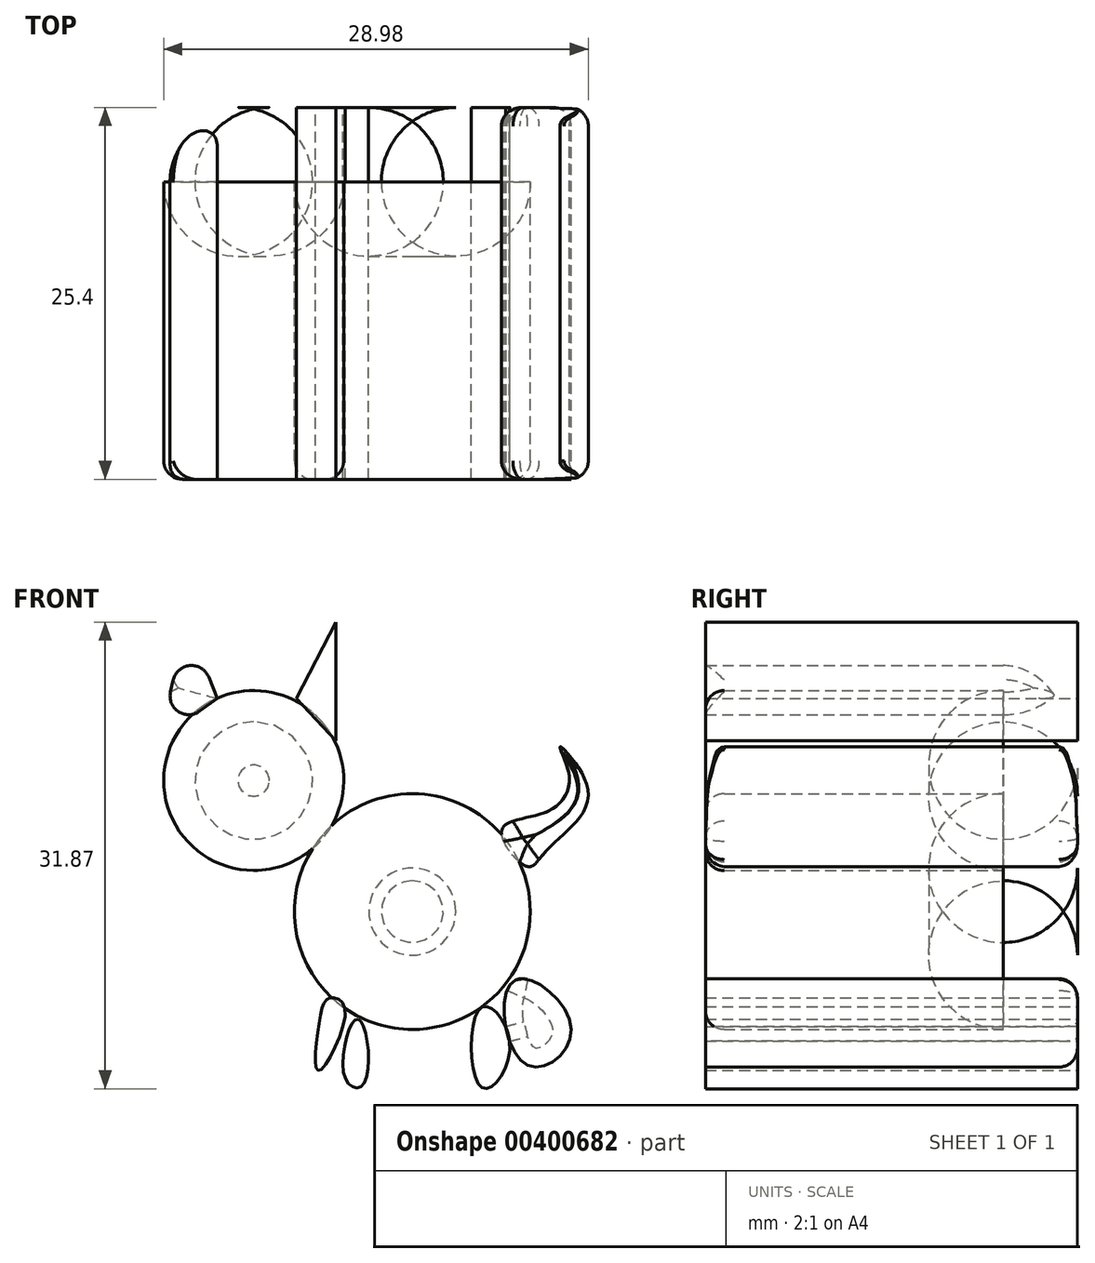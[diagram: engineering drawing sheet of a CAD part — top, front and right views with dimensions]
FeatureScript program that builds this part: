
annotation { "Feature Type Name" : "Feature", "Feature Type Description" : "" }
export const myFeature = defineFeature(function(context is Context, id is Id, definition is map)
    precondition{}
    {
        {
            var Q0;
            Q0=qCreatedBy(makeId("Front.planeOp"),FACE);
            var sketch = newSketch(context, id + "F0", { "sketchPlane" : qUnion([Q0])});
            skCircle(sketch, "E0", {"center": v(-53.48, 46.1) * mm, "radius": 6.14 * mm});
            skSolve(sketch);
        }
        {
            var Q0;
            Q0=qCreatedBy(makeId("Front.planeOp"),FACE);
            var sketch = newSketch(context, id + "F1", { "sketchPlane" : qUnion([Q0])});
            skLineSegment(sketch, "E1", {"start": v(-50.57, 51.7) * mm, "end": v(-47.86, 56.91) * mm});
            skLineSegment(sketch, "E2", {"start": v(-47.86, 48.8) * mm, "end": v(-47.86, 56.91) * mm});
            skLineSegment(sketch, "E3", {"start": v(-50.57, 51.7) * mm, "end": v(-47.86, 48.8) * mm});
            skLineSegment(sketch, "E4", {"start": v(-55.98, 51.7) * mm, "end": v(-58.06, 56.91) * mm});
            skLineSegment(sketch, "E5", {"start": v(-58.06, 56.91) * mm, "end": v(-59.93, 48.8) * mm});
            skLineSegment(sketch, "E6", {"start": v(-59.93, 48.8) * mm, "end": v(-55.98, 51.7) * mm});
            skSolve(sketch);
        }
        {
            var Q0;
            Q0=qCreatedBy(makeId("Front.planeOp"),FACE);
            var sketch = newSketch(context, id + "F2", { "sketchPlane" : qUnion([Q0])});
            skCircle(sketch, "E7", {"center": v(-42.65, 37.14) * mm, "radius": 8.05 * mm});
            skSolve(sketch);
        }
        {
            var Q0;
            Q0=qCreatedBy(makeId("Front.planeOp"),FACE);
            var sketch = newSketch(context, id + "F3", { "sketchPlane" : qUnion([Q0])});
            skFitSpline(sketch, "E8", {"points": [v(-48.28, 31.24) * mm, v(-48.97, 29.8) * mm, v(-49.04, 26.3) * mm, v(-47.25, 30.55) * mm, v(-48.28, 31.24) * mm]});
            skFitSpline(sketch, "E9", {"points": [v(-46.36, 29.8) * mm, v(-47.25, 25.81) * mm, v(-45.95, 25.4) * mm, v(-46.36, 29.8) * mm]});
            skFitSpline(sketch, "E10", {"points": [v(-37.98, 30.55) * mm, v(-37.92, 25.13) * mm, v(-36, 28) * mm, v(-37.98, 30.55) * mm]});
            skFitSpline(sketch, "E11", {"points": [v(-35.72, 32.4) * mm, v(-34.9, 26.7) * mm, v(-31.8, 29.1) * mm, v(-35.72, 32.4) * mm]});
            skFitSpline(sketch, "E12", {"points": [v(-36.54, 42.7) * mm, v(-33.52, 43.94) * mm, v(-31.94, 46.4) * mm, v(-32.56, 48.4) * mm, v(-30.91, 46.27) * mm, v(-31.12, 43.73) * mm, v(-33.73, 41.05) * mm, v(-34.83, 40.23) * mm, v(-36.54, 42.7) * mm]});
            skSolve(sketch);
        }
        {
            var Q0;
            Q0=makeQuery(id+"F1.imprint","IMPRINT",FACE,{"disambiguationData":[TD([[makeQuery(id+"F1.imprint","IMPRINT",EDGE,{"derivedFrom":sQuery(id+"F1.wireOp",EDGE,"E4")}),1.0]])]});
            var Q1;
            Q1=makeQuery(id+"F1.imprint","IMPRINT",FACE,{"disambiguationData":[TD([[makeQuery(id+"F1.imprint","IMPRINT",EDGE,{"derivedFrom":sQuery(id+"F1.wireOp",EDGE,"E1")}),-1.0]])]});
            var Q2;
            Q2=makeQuery(id+"F2.imprint","IMPRINT",FACE,{"disambiguationData":[TD([[makeQuery(id+"F2.imprint","IMPRINT",EDGE,{"derivedFrom":sQuery(id+"F2.wireOp",EDGE,"E7")}),1.0]])]});
            var Q3;
            Q3=makeQuery(id+"F3.imprint","IMPRINT",FACE,{"disambiguationData":[TD([[makeQuery(id+"F3.imprint","IMPRINT",EDGE,{"derivedFrom":sQuery(id+"F3.wireOp",EDGE,"E8")}),1.0]])]});
            var Q4;
            Q4=makeQuery(id+"F3.imprint","IMPRINT",FACE,{"disambiguationData":[TD([[makeQuery(id+"F3.imprint","IMPRINT",EDGE,{"derivedFrom":sQuery(id+"F3.wireOp",EDGE,"E9")}),1.0]])]});
            var Q5;
            {var subQ0=sQuery(id+"F3.wireOp",EDGE,"E11");var subQ1=sQuery(id+"F3.wireOp",EDGE,"E10");var subQ2=makeQuery(id+"F3.imprint","INTERSECT",VERTEX,{"disambiguationData":[OD(0.0)],"derivedFrom":[subQ1,subQ0]});Q5=makeQuery(id+"F3.imprint","IMPRINT",FACE,{"disambiguationData":[TD([[makeQuery(id+"F3.imprint","IMPRINT",EDGE,{"disambiguationData":[TD([[subQ2,1.0]])],"derivedFrom":subQ1}),1.0]])]});}
            var Q6;
            {var subQ0=sQuery(id+"F3.wireOp",EDGE,"E11");var subQ1=sQuery(id+"F3.wireOp",EDGE,"E10");var subQ2=makeQuery(id+"F3.imprint","INTERSECT",VERTEX,{"disambiguationData":[OD(0.0)],"derivedFrom":[subQ1,subQ0]});Q6=makeQuery(id+"F3.imprint","IMPRINT",FACE,{"disambiguationData":[TD([[makeQuery(id+"F3.imprint","IMPRINT",EDGE,{"disambiguationData":[TD([[subQ2,-1.0]])],"derivedFrom":subQ1}),-1.0]])]});}
            var Q7;
            Q7=makeQuery(id+"F3.imprint","IMPRINT",FACE,{"disambiguationData":[TD([[makeQuery(id+"F3.imprint","IMPRINT",EDGE,{"derivedFrom":sQuery(id+"F3.wireOp",EDGE,"E12")}),-1.0]])]});
            var Q8;
            Q8=makeQuery(id+"F0.imprint","IMPRINT",FACE,{"disambiguationData":[TD([[makeQuery(id+"F0.imprint","IMPRINT",EDGE,{"derivedFrom":sQuery(id+"F0.wireOp",EDGE,"E0")}),1.0]])]});
            extrude(context, id + "F4", {"entities" : qUnion([Q0, Q1, Q2, Q3, Q4, Q5, Q6, Q7, Q8]), "depth" : 25.4 * mm});
        }
        {
            var Q0;
            Q0=makeQuery(id+"F4.opExtrude","CAP_FACE",FACE,{"disambiguationData":[OSD([sQuery(id+"F2.wireOp",EDGE,"E7")])],"isStart":true});
            var Q1;
            Q1=makeQuery(id+"F4.opExtrude","CAP_FACE",FACE,{"disambiguationData":[OSD([sQuery(id+"F3.wireOp",EDGE,"E12")])],"isStart":true});
            var Q2;
            Q2=makeQuery(id+"F4.opExtrude","CAP_FACE",FACE,{"disambiguationData":[OSD([sQuery(id+"F0.wireOp",EDGE,"E0")])],"isStart":true});
            var Q3;
            Q3=makeQuery(id+"F4.opExtrude","CAP_EDGE",EDGE,{"disambiguationData":[OSD([sQuery(id+"F1.wireOp",EDGE,"E1")])],"isStart":true});
            var Q4;
            Q4=makeQuery(id+"F4.opExtrude","CAP_FACE",FACE,{"disambiguationData":[OSD([sQuery(id+"F1.wireOp",EDGE,"E1"),sQuery(id+"F1.wireOp",EDGE,"E2"),sQuery(id+"F1.wireOp",EDGE,"E3")])],"isStart":true});
            var Q5;
            Q5=makeQuery(id+"F4.opExtrude","CAP_EDGE",EDGE,{"disambiguationData":[OSD([sQuery(id+"F1.wireOp",EDGE,"E5")])],"isStart":true});
            var Q6;
            Q6=makeQuery(id+"F4.opExtrude","CAP_EDGE",EDGE,{"disambiguationData":[OSD([sQuery(id+"F3.wireOp",EDGE,"E8")])],"isStart":true});
            var Q7;
            Q7=makeQuery(id+"F4.opExtrude","CAP_EDGE",EDGE,{"disambiguationData":[OSD([sQuery(id+"F3.wireOp",EDGE,"E9")])],"isStart":true});
            var Q8;
            {var subQ0=sQuery(id+"F3.wireOp",EDGE,"E11");var subQ1=sQuery(id+"F3.wireOp",EDGE,"E10");var subQ2=makeQuery(id+"F3.imprint","INTERSECT",VERTEX,{"disambiguationData":[OD(0.0)],"derivedFrom":[subQ1,subQ0]});Q8=makeQuery(id+"F4.opExtrude","CAP_FACE",FACE,{"disambiguationData":[OSD([subQ1,subQ0]),TDD([makeQuery(id+"F3.imprint","IMPRINT",EDGE,{"disambiguationData":[TD([[subQ2,1.0]])],"derivedFrom":subQ1}),makeQuery(id+"F3.imprint","IMPRINT",EDGE,{"disambiguationData":[TD([[subQ2,1.0]])],"derivedFrom":subQ0})])],"isStart":true});}
            var Q9;
            {var subQ0=sQuery(id+"F3.wireOp",EDGE,"E11");var subQ1=sQuery(id+"F3.wireOp",EDGE,"E10");var subQ2=makeQuery(id+"F3.imprint","INTERSECT",VERTEX,{"disambiguationData":[OD(0.0)],"derivedFrom":[subQ1,subQ0]});Q9=makeQuery(id+"F4.opExtrude","CAP_FACE",FACE,{"disambiguationData":[OSD([subQ1,subQ0]),TDD([makeQuery(id+"F3.imprint","IMPRINT",EDGE,{"disambiguationData":[TD([[subQ2,-1.0]])],"derivedFrom":subQ1}),makeQuery(id+"F3.imprint","IMPRINT",EDGE,{"disambiguationData":[TD([[subQ2,-1.0]])],"derivedFrom":subQ0})])],"isStart":true});}
            fillet(context, id + "F5", {"entities" : qUnion([Q0, Q1, Q2, Q3, Q4, Q5, Q6, Q7, Q8, Q9]), "radius" : 5.08 * mm, "tangentPropagation" : true, "allowEdgeOverflow" : false});
        }
        {
            var Q0;
            {var subQ0=sQuery(id+"F3.wireOp",EDGE,"E11");var subQ1=sQuery(id+"F3.wireOp",EDGE,"E10");var subQ2=makeQuery(id+"F3.imprint","INTERSECT",VERTEX,{"disambiguationData":[OD(0.0)],"derivedFrom":[subQ1,subQ0]});Q0=makeQuery(id+"F4.opExtrude","CAP_FACE",FACE,{"disambiguationData":[OSD([subQ1,subQ0]),TDD([makeQuery(id+"F3.imprint","IMPRINT",EDGE,{"disambiguationData":[TD([[subQ2,-1.0]])],"derivedFrom":subQ1}),makeQuery(id+"F3.imprint","IMPRINT",EDGE,{"disambiguationData":[TD([[subQ2,-1.0]])],"derivedFrom":subQ0})])],"isStart":true});}
            var Q1;
            {var subQ0=sQuery(id+"F3.wireOp",EDGE,"E11");var subQ1=sQuery(id+"F3.wireOp",EDGE,"E10");Q1=makeQuery(id+"F4.opExtrude","CAP_EDGE",EDGE,{"disambiguationData":[OSD([subQ1]),TDD([makeQuery(id+"F3.imprint","IMPRINT",EDGE,{"disambiguationData":[TD([[makeQuery(id+"F3.imprint","INTERSECT",VERTEX,{"disambiguationData":[OD(0.0)],"derivedFrom":[subQ1,subQ0]}),1.0]])],"derivedFrom":subQ1})])],"isStart":true});}
            var Q2;
            Q2=makeQuery(id+"F4.opExtrude","CAP_FACE",FACE,{"disambiguationData":[OSD([sQuery(id+"F2.wireOp",EDGE,"E7")])],"isStart":true});
            var Q3;
            Q3=makeQuery(id+"F4.opExtrude","SWEPT_FACE",FACE,{"disambiguationData":[OSD([sQuery(id+"F3.wireOp",EDGE,"E12")])]});
            var Q4;
            Q4=makeQuery(id+"F4.opExtrude","CAP_FACE",FACE,{"disambiguationData":[OSD([sQuery(id+"F3.wireOp",EDGE,"E12")])],"isStart":true});
            var Q5;
            Q5=makeQuery(id+"F4.opExtrude","SWEPT_FACE",FACE,{"disambiguationData":[OSD([sQuery(id+"F0.wireOp",EDGE,"E0")])]});
            var Q6;
            Q6=makeQuery(id+"F4.opExtrude","SWEPT_FACE",FACE,{"disambiguationData":[OSD([sQuery(id+"F1.wireOp",EDGE,"E5")])]});
            var Q7;
            Q7=makeQuery(id+"F4.opExtrude","SWEPT_FACE",FACE,{"disambiguationData":[OSD([sQuery(id+"F1.wireOp",EDGE,"E1")])]});
            var Q8;
            Q8=makeQuery(id+"F4.opExtrude","SWEPT_FACE",FACE,{"disambiguationData":[OSD([sQuery(id+"F3.wireOp",EDGE,"E8")])]});
            var Q9;
            Q9=makeQuery(id+"F4.opExtrude","SWEPT_FACE",FACE,{"disambiguationData":[OSD([sQuery(id+"F3.wireOp",EDGE,"E9")])]});
            var Q10;
            {var subQ0=sQuery(id+"F3.wireOp",EDGE,"E11");var subQ1=sQuery(id+"F3.wireOp",EDGE,"E10");Q10=makeQuery(id+"F4.opExtrude","SWEPT_FACE",FACE,{"disambiguationData":[OSD([subQ1]),TDD([makeQuery(id+"F3.imprint","IMPRINT",EDGE,{"disambiguationData":[TD([[makeQuery(id+"F3.imprint","INTERSECT",VERTEX,{"disambiguationData":[OD(0.0)],"derivedFrom":[subQ1,subQ0]}),1.0]])],"derivedFrom":subQ1})])]});}
            var Q11;
            Q11=makeQuery(id+"F4.opExtrude","SWEPT_FACE",FACE,{"disambiguationData":[OSD([sQuery(id+"F2.wireOp",EDGE,"E7")])]});
            var Q12;
            Q12=makeQuery(id+"F4.opExtrude","CAP_FACE",FACE,{"disambiguationData":[OSD([sQuery(id+"F1.wireOp",EDGE,"E1"),sQuery(id+"F1.wireOp",EDGE,"E2"),sQuery(id+"F1.wireOp",EDGE,"E3")])],"isStart":true});
            fillet(context, id + "F6", {"entities" : qUnion([Q0, Q1, Q2, Q3, Q4, Q5, Q6, Q7, Q8, Q9, Q10, Q11, Q12]), "radius" : 1.27 * mm, "tangentPropagation" : true, "allowEdgeOverflow" : false});
        }
    });
